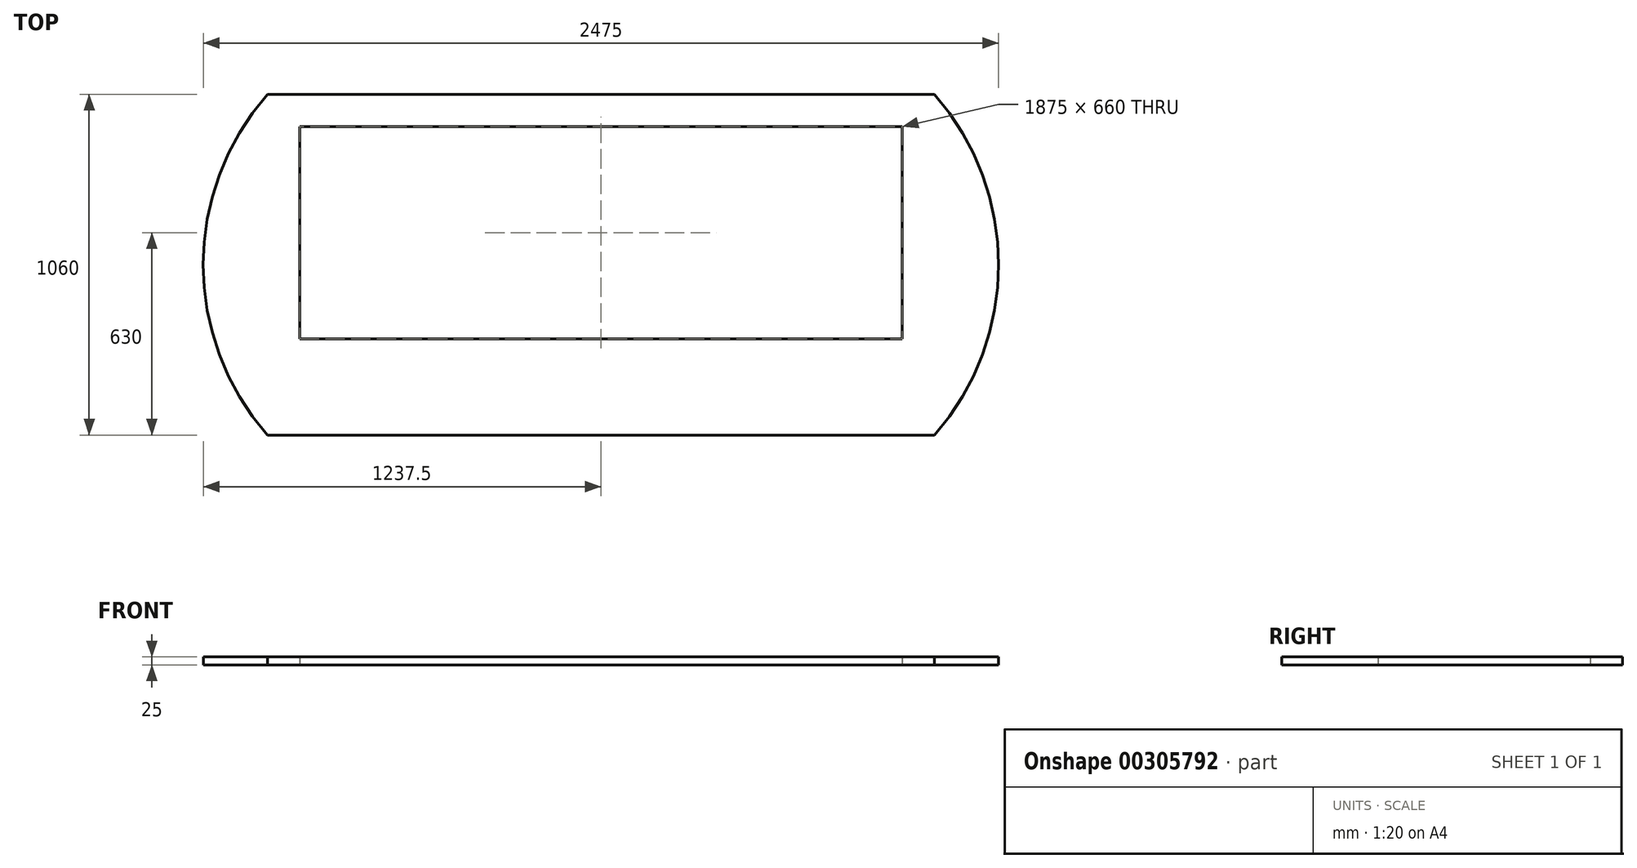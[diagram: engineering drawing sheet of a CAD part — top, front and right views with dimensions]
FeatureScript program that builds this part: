
annotation { "Feature Type Name" : "Feature", "Feature Type Description" : "" }
export const myFeature = defineFeature(function(context is Context, id is Id, definition is map)
    precondition{}
    {
        {
            var Q0;
            Q0=qCreatedBy(makeId("Top.planeOp"),FACE);
            var sketch = newSketch(context, id + "F0", { "sketchPlane" : qUnion([Q0])});
            skLineSegment(sketch, "E0.bottom", {"start": v(937.5, 330) * mm, "end": v(-937.5, 330) * mm});
            skLineSegment(sketch, "E0.top", {"start": v(937.5, -330) * mm, "end": v(-937.5, -330) * mm});
            skLineSegment(sketch, "E0.left", {"start": v(937.5, 330) * mm, "end": v(937.5, -330) * mm});
            skLineSegment(sketch, "E0.right", {"start": v(-937.5, 330) * mm, "end": v(-937.5, -330) * mm});
            skPoint(sketch, "E0.middle", {"position": v(0, 0) * mm});
            skLineSegment(sketch, "E1", {"start": v(-1037.5, 430) * mm, "end": v(1037.5, 430) * mm});
            skLineSegment(sketch, "E2", {"start": v(-1037.5, -630) * mm, "end": v(1037.5, -630) * mm});
            skArc(sketch, "E3", {"start": v(1037.5, -630) * mm, "mid": v(1237.5, -100) * mm, "end": v(1037.5, 430) * mm});
            skArc(sketch, "E4", {"start": v(-1037.5, 430) * mm, "mid": v(-1237.5, -100) * mm, "end": v(-1037.5, -630) * mm});
            skSolve(sketch);
        }
        {
            var Q0;
            Q0 = qSketchRegion(id + "F0", true);
            extrude(context, id + "F1", {"entities" : qUnion([Q0]), "depth" : 25 * mm});
        }
    });
